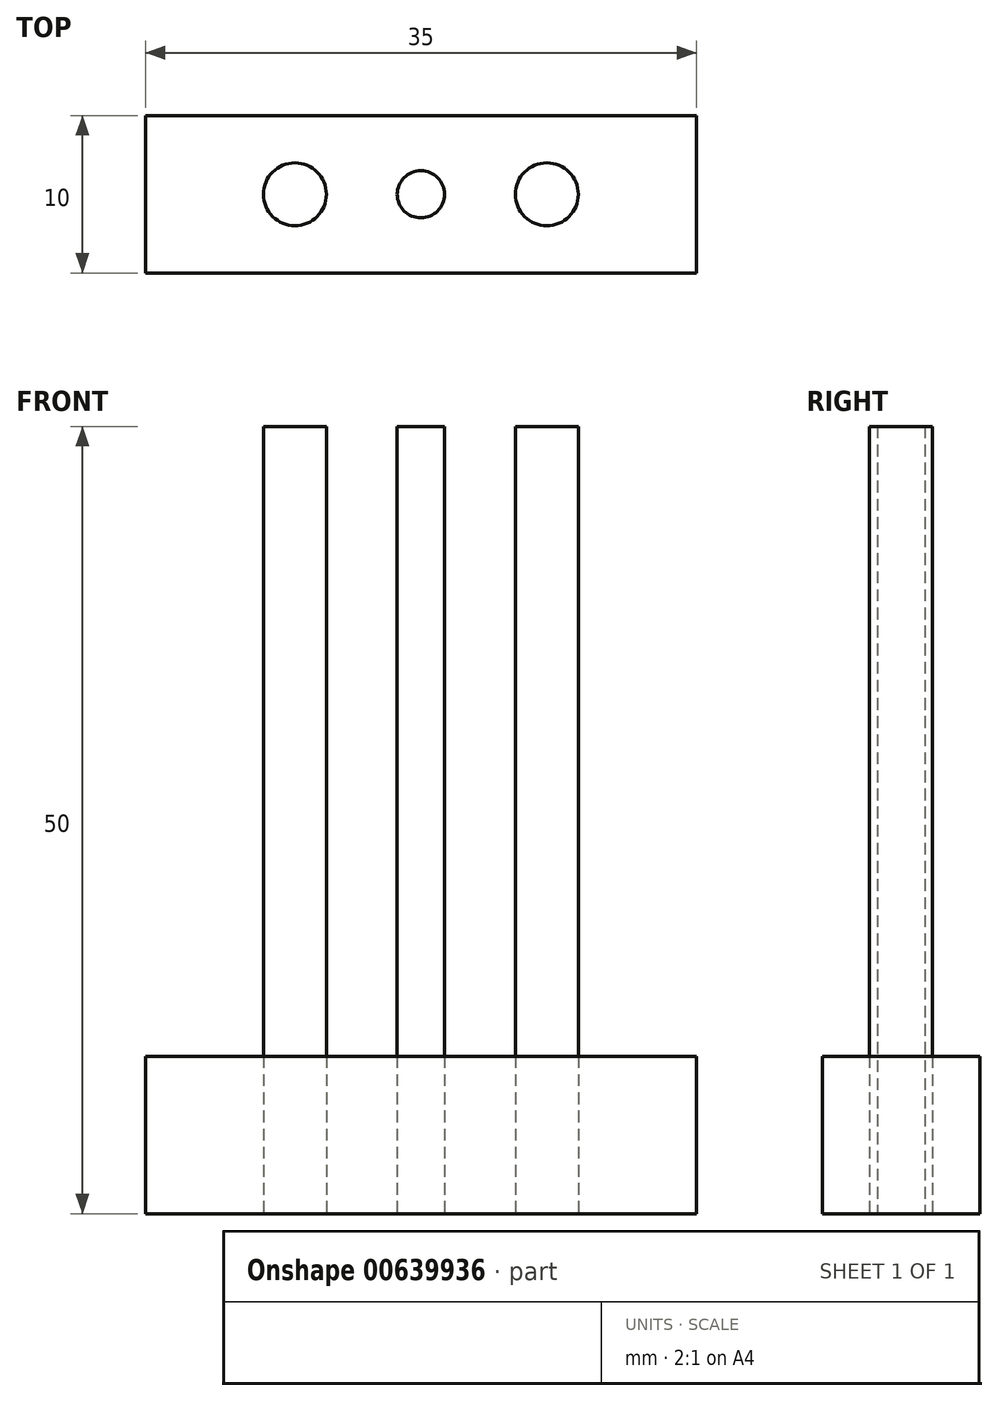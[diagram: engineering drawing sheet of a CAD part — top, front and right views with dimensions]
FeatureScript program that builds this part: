
annotation { "Feature Type Name" : "Feature", "Feature Type Description" : "" }
export const myFeature = defineFeature(function(context is Context, id is Id, definition is map)
    precondition{}
    {
        {
            var Q0;
            Q0=qCreatedBy(makeId("Top.planeOp"),FACE);
            var sketch = newSketch(context, id + "F0", { "sketchPlane" : qUnion([Q0])});
            skCircle(sketch, "E0", {"center": v(9.5, 0) * mm, "radius": 2 * mm});
            skCircle(sketch, "E1", {"center": v(17.5, 0) * mm, "radius": 1.5 * mm});
            skCircle(sketch, "E2", {"center": v(25.5, 0) * mm, "radius": 2 * mm});
            skSolve(sketch);
        }
        {
            var Q0;
            Q0 = qSketchRegion(id + "F0", true);
            extrude(context, id + "F1", {"entities" : qUnion([Q0]), "depth" : 50 * mm, "offsetDistance" : 25 * mm});
        }
        {
            var Q0;
            Q0=qCreatedBy(makeId("Top.planeOp"),FACE);
            var sketch = newSketch(context, id + "F2", { "sketchPlane" : qUnion([Q0])});
            skLineSegment(sketch, "E3.bottom", {"start": v(0, 5) * mm, "end": v(35, 5) * mm});
            skLineSegment(sketch, "E3.top", {"start": v(0, -5) * mm, "end": v(35, -5) * mm});
            skLineSegment(sketch, "E3.left", {"start": v(0, 5) * mm, "end": v(0, -5) * mm});
            skLineSegment(sketch, "E3.right", {"start": v(35, 5) * mm, "end": v(35, -5) * mm});
            skSolve(sketch);
        }
        {
            var Q0;
            Q0 = qSketchRegion(id + "F2", true);
            extrude(context, id + "F3", {"entities" : qUnion([Q0]), "depth" : 10 * mm, "offsetDistance" : 25 * mm});
        }
    });
